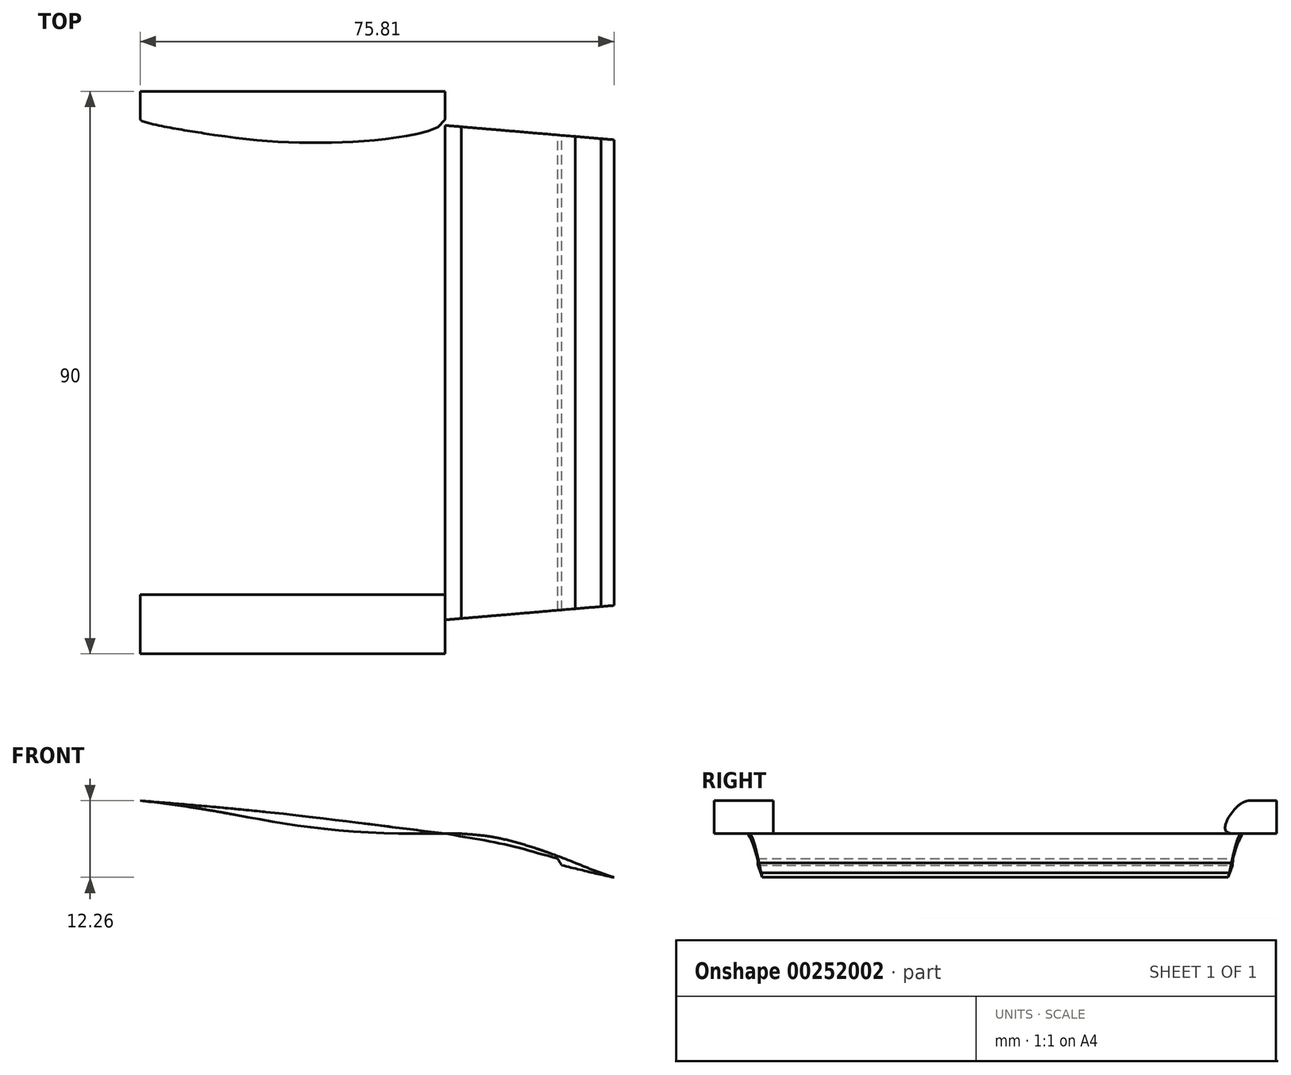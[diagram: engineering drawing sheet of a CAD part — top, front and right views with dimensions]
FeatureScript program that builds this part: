
annotation { "Feature Type Name" : "Feature", "Feature Type Description" : "" }
export const myFeature = defineFeature(function(context is Context, id is Id, definition is map)
    precondition{}
    {
        {
            var Q0;
            Q0=qCreatedBy(makeId("Top.planeOp"),FACE);
            var sketch = newSketch(context, id + "F0", { "sketchPlane" : qUnion([Q0])});
            skLineSegment(sketch, "E0.left", {"start": v(51.5, 37) * mm, "end": v(51.5, -37) * mm});
            skLineSegment(sketch, "E0.right", {"start": v(-51.5, 37) * mm, "end": v(-51.5, 35) * mm});
            skPoint(sketch, "E0.middle", {"position": v(0, 0) * mm});
            skLineSegment(sketch, "E1.bottom", {"start": v(-51.5, 35) * mm, "end": v(-24.5, 35) * mm});
            skLineSegment(sketch, "E1.top", {"start": v(-51.5, -35) * mm, "end": v(-24.5, -35) * mm});
            skLineSegment(sketch, "E1.right", {"start": v(-24.5, 35) * mm, "end": v(-24.5, -35) * mm});
            skPoint(sketch, "E1.middle", {"position": v(-38, 0) * mm});
            skLineSegment(sketch, "E2.trimOffspring", {"start": v(-51.5, -35) * mm, "end": v(-51.5, -37) * mm});
            skLineSegment(sketch, "E3", {"start": v(-36.5, 44.5) * mm, "end": v(51.5, 37) * mm});
            skLineSegment(sketch, "E4", {"start": v(-36.5, -44.5) * mm, "end": v(51.5, -37) * mm});
            skLineSegment(sketch, "E5", {"start": v(-36.5, 44.5) * mm, "end": v(-51.5, 44.5) * mm});
            skLineSegment(sketch, "E6", {"start": v(-51.5, 44.5) * mm, "end": v(-51.5, 37) * mm});
            skLineSegment(sketch, "E7", {"start": v(-51.5, -37) * mm, "end": v(-51.5, -44.5) * mm});
            skLineSegment(sketch, "E8", {"start": v(-51.5, -44.5) * mm, "end": v(-36.5, -44.5) * mm});
            skSolve(sketch);
        }
        {
            var Q0;
            Q0=makeQuery(id+"F0.imprint","IMPRINT",FACE,{"disambiguationData":[TD([[makeQuery(id+"F0.imprint","IMPRINT",EDGE,{"derivedFrom":sQuery(id+"F0.wireOp",EDGE,"E0.left")}),-1.0]])]});
            extrude(context, id + "F1", {"entities" : qUnion([Q0]), "endBound" : BoundingType.SYMMETRIC, "depth" : 40 * mm});
        }
        {
            var Q0;
            Q0=qCreatedBy(makeId("Front.planeOp"),FACE);
            var sketch = newSketch(context, id + "F2", { "sketchPlane" : qUnion([Q0])});
            skLineSegment(sketch, "E9", {"start": v(-51.5, -30.88) * mm, "end": v(-51.5, 38.27) * mm, "construction": true});
            skArc(sketch, "E10", {"start": v(-35.08, 14.93) * mm, "mid": v(-51.27, -2.64) * mm, "end": v(-30, -13.52) * mm});
            skLineSegment(sketch, "E11", {"start": v(21.5, 0) * mm, "end": v(66.36, 0) * mm, "construction": true});
            skLineSegment(sketch, "E12", {"start": v(21.5, 29.58) * mm, "end": v(21.5, -38.08) * mm, "construction": true});
            skLineSegment(sketch, "E13", {"start": v(13.3, 4) * mm, "end": v(21.47, 4) * mm, "construction": true});
            skLineSegment(sketch, "E14", {"start": v(39.5, 24.03) * mm, "end": v(39.5, -41.22) * mm, "construction": true});
            skPoint(sketch, "E15.orphan", {"position": v(0, 0) * mm});
            skFitSpline(sketch, "E16", {"points": [v(-31.64, -14.2) * mm, v(21.5, 4) * mm], "startDerivative": vector(84.94, 34.81) * mm, "endDerivative": vector(74.48, 19.76) * mm});
            skFitSpline(sketch, "E17", {"points": [v(21.5, 4) * mm, v(39.5, 0) * mm], "startDerivative": vector(28.2, -4.73) * mm, "endDerivative": vector(25.8, -7.27) * mm});
            skArc(sketch, "E18", {"start": v(50.52, -2.49) * mm, "mid": v(51.49, -0.27) * mm, "end": v(50.14, 1.73) * mm});
            skArc(sketch, "E19", {"start": v(39.5, 0) * mm, "mid": v(44.43, -3.82) * mm, "end": v(50.52, -2.49) * mm});
            skPoint(sketch, "E19.second.point", {"position": v(50.23, -2.7) * mm});
            skPoint(sketch, "E19.third.point", {"position": v(51.49, 8.31) * mm});
            skLineSegment(sketch, "E20", {"start": v(10.87, 9) * mm, "end": v(35.57, 9) * mm, "construction": true});
            skFitSpline(sketch, "E21.0", {"points": [v(21.5, 4) * mm, v(24.08, 4) * mm, v(28.98, 3.5) * mm, v(35.82, 1.7) * mm, v(42.27, -0.66) * mm, v(46.42, -2.27) * mm, v(48.5, -3) * mm]});
            skFitSpline(sketch, "E21.1", {"points": [v(-35.45, 9.95) * mm, v(-31.94, 9.69) * mm, v(-25.87, 9.12) * mm, v(-18.84, 8.18) * mm, v(-13.14, 7.2) * mm, v(-7.95, 6.24) * mm, v(-2.55, 5.34) * mm, v(3.68, 4.6) * mm, v(11.32, 4.12) * mm, v(17.8, 4) * mm, v(21.5, 4) * mm]});
            skFitSpline(sketch, "E22.trimOffspring", {"points": [v(21.5, 4) * mm, v(24.08, 4) * mm, v(28.98, 3.5) * mm, v(35.82, 1.7) * mm, v(42.27, -0.66) * mm, v(46.42, -2.27) * mm, v(48.5, -3) * mm, v(21.5, 4) * mm]});
            skLineSegment(sketch, "E23", {"start": v(-21.5, 30.5) * mm, "end": v(-21.5, -32.58) * mm, "construction": true});
            skLineSegment(sketch, "E24", {"start": v(-16.5, 19.65) * mm, "end": v(-16.5, 3.36) * mm, "construction": true});
            skLineSegment(sketch, "E25", {"start": v(-21.5, 13.8) * mm, "end": v(-17.04, 8.4) * mm});
            skFitSpline(sketch, "E26", {"points": [v(-35.08, 14.93) * mm, v(21.5, 9) * mm], "startDerivative": vector(86.4, -7.05) * mm, "endDerivative": vector(83.38, -10.43) * mm});
            skFitSpline(sketch, "E27", {"points": [v(21.5, 9) * mm, v(50.14, 1.73) * mm], "startDerivative": vector(37.32, -4.67) * mm, "endDerivative": vector(8.35, -5.74) * mm});
            skFitSpline(sketch, "E28.trimOffspring", {"points": [v(-34.87, 9.89) * mm, v(-27.67, 9.3) * mm, v(-19.58, 8.64) * mm, v(-11.59, 7.9) * mm, v(-6.32, 7.37) * mm, v(-1.09, 6.8) * mm, v(6.73, 5.85) * mm, v(14.55, 4.87) * mm, v(21.5, 4) * mm]});
            skLineSegment(sketch, "E29.trimOffspring", {"start": v(21.5, 4) * mm, "end": v(34.75, 4) * mm, "construction": true});
            skSolve(sketch);
        }
        {
            var Q0;
            {var subQ0=sQuery(id+"F2.wireOp",EDGE,"E28.trimOffspring");Q0=makeQuery(id+"F2.imprint","IMPRINT",FACE,{"disambiguationData":[TD([[makeQuery(id+"F2.imprint","IMPRINT",EDGE,{"derivedFrom":subQ0}),-1.0]])]});}
            var Q1;
            Q1=makeQuery(id+"F2.imprint","IMPRINT",FACE,{"disambiguationData":[TD([[makeQuery(id+"F2.imprint","IMPRINT",EDGE,{"derivedFrom":sQuery(id+"F2.wireOp",EDGE,"E17")}),1.0]])]});
            extrude(context, id + "F3", {"entities" : qUnion([Q0, Q1]), "endBound" : BoundingType.SYMMETRIC, "depth" : 90 * mm});
        }
        {
            var Q0;
            Q0=makeQuery(id+"F1.opExtrude","SWEPT_BODY",BODY,{"disambiguationData":[OSD([sQuery(id+"F0.wireOp",EDGE,"E0.left"),sQuery(id+"F0.wireOp",EDGE,"E0.right"),sQuery(id+"F0.wireOp",EDGE,"E1.bottom"),sQuery(id+"F0.wireOp",EDGE,"E1.top"),sQuery(id+"F0.wireOp",EDGE,"E1.right"),sQuery(id+"F0.wireOp",EDGE,"E2.trimOffspring"),sQuery(id+"F0.wireOp",EDGE,"E3"),sQuery(id+"F0.wireOp",EDGE,"E4"),sQuery(id+"F0.wireOp",EDGE,"E5"),sQuery(id+"F0.wireOp",EDGE,"E6"),sQuery(id+"F0.wireOp",EDGE,"E7"),sQuery(id+"F0.wireOp",EDGE,"E8")])]});
            var Q1;
            Q1=makeQuery(id+"F3.opExtrude","SWEPT_BODY",BODY,{"disambiguationData":[OSD([sQuery(id+"F2.wireOp",EDGE,"E10"),sQuery(id+"F2.wireOp",EDGE,"E16"),sQuery(id+"F2.wireOp",EDGE,"E17"),sQuery(id+"F2.wireOp",EDGE,"E18"),sQuery(id+"F2.wireOp",EDGE,"E19"),sQuery(id+"F2.wireOp",EDGE,"15d79667-4b94-408e-8f36-41715205f070"),sQuery(id+"F2.wireOp",EDGE,"74bc5fd0-7af1-4538-94f5-d98413db5bcc")])]});
            booleanBodies(context, id + "F4", {"operationType" : BooleanOperationType.INTERSECTION, "tools" : qUnion([Q0, Q1])});
        }
        {
            var Q0;
            {var subQ0=sQuery(id+"F2.wireOp",EDGE,"E28.trimOffspring");Q0=makeQuery(id+"F2.imprint","IMPRINT",FACE,{"disambiguationData":[TD([[makeQuery(id+"F2.imprint","IMPRINT",EDGE,{"derivedFrom":subQ0}),-1.0]])]});}
            extrude(context, id + "F5", {"entities" : qUnion([Q0]), "operationType" : NewBodyOperationType.REMOVE, "endBound" : BoundingType.SYMMETRIC, "oppositeDirection" : true, "depth" : 71 * mm});
        }
        {
            var Q0;
            Q0=qCreatedBy(makeId("Front.planeOp"),FACE);
            var sketch = newSketch(context, id + "F6", { "sketchPlane" : qUnion([Q0])});
            skArc(sketch, "E30.0", {"start": v(-35.08, 14.93) * mm, "mid": v(-51.27, -2.64) * mm, "end": v(-30, -13.52) * mm});
            skLineSegment(sketch, "E31", {"start": v(-36.5, 0) * mm, "end": v(-62.57, 0) * mm, "construction": true});
            skLineSegment(sketch, "E32", {"start": v(-36.5, 0) * mm, "end": v(-67.58, -11.93) * mm, "construction": true});
            skLineSegment(sketch, "E33", {"start": v(-51.5, 0) * mm, "end": v(-50.5, -5.38) * mm, "construction": true});
            skArc(sketch, "E34", {"start": v(-24.55, 1.05) * mm, "mid": v(-25.3, 4.3) * mm, "end": v(-26.91, 7.22) * mm});
            skLineSegment(sketch, "E35", {"start": v(-36.5, 0) * mm, "end": v(-28.49, -18.8) * mm, "construction": true});
            skLineSegment(sketch, "E36", {"start": v(-25.29, 7.84) * mm, "end": v(-29.43, 6.25) * mm, "construction": true});
            skLineSegment(sketch, "E37", {"start": v(-23.12, 1.6) * mm, "end": v(-28.08, -0.3) * mm, "construction": true});
            skLineSegment(sketch, "E38", {"start": v(-54.32, -2.77) * mm, "end": v(-47.19, -0.03) * mm, "construction": true});
            skLineSegment(sketch, "E39", {"start": v(-44.94, -7.31) * mm, "end": v(-52.1, -10.06) * mm, "construction": true});
            skLineSegment(sketch, "E40", {"start": v(-51.4, -1.65) * mm, "end": v(-26.91, 7.22) * mm});
            skLineSegment(sketch, "E41", {"start": v(-24.55, 1.05) * mm, "end": v(-48.69, -8.75) * mm});
            skSolve(sketch);
        }
        {
            var Q0;
            Q0=makeQuery(id+"F6.imprint","IMPRINT",FACE,{"disambiguationData":[TD([[makeQuery(id+"F6.imprint","IMPRINT",EDGE,{"derivedFrom":sQuery(id+"F6.wireOp",EDGE,"E34")}),1.0]])]});
            extrude(context, id + "F7", {"entities" : qUnion([Q0]), "operationType" : NewBodyOperationType.REMOVE, "endBound" : BoundingType.SYMMETRIC, "oppositeDirection" : true, "depth" : 83.5 * mm});
        }
        {
            var Q0;
            Q0=sQuery(id+"F6.wireOp",EDGE,"E32");
            cPlane(context, id + "F8", {"entities" : qUnion([Q0]), "cplaneType" : CPlaneType.LINE_ANGLE, "offset" : 25 * mm, "angle" : 90 * degree, "width" : 150 * mm, "height" : 150 * mm});
        }
        {
            var Q0;
            Q0=qCreatedBy(id+"F8.planeOp",FACE);
            var sketch = newSketch(context, id + "F9", { "sketchPlane" : qUnion([Q0])});
            skLineSegment(sketch, "E42", {"start": v(-33.58, 0) * mm, "end": v(-33.58, -28.28) * mm, "construction": true});
            skLineSegment(sketch, "E43", {"start": v(-33.58, -39) * mm, "end": v(-33.58, 39) * mm, "construction": true});
            skCircle(sketch, "E44", {"center": v(-33.58, 39) * mm, "radius": 1.25 * mm});
            skCircle(sketch, "E45", {"center": v(-33.58, -39) * mm, "radius": 1.25 * mm});
            skSolve(sketch);
        }
        {
            var Q0;
            Q0 = qSketchRegion(id + "F9", true);
            extrude(context, id + "F10", {"entities" : qUnion([Q0]), "operationType" : NewBodyOperationType.REMOVE, "oppositeDirection" : true, "depth" : 25 * mm});
        }
        {
            var Q0;
            Q0=sQuery(id+"F6.wireOp",EDGE,"E35");
            cPlane(context, id + "F11", {"entities" : qUnion([Q0]), "cplaneType" : CPlaneType.LINE_ANGLE, "offset" : 25 * mm, "angle" : 0 * degree, "width" : 150 * mm, "height" : 150 * mm});
        }
        {
            var Q0;
            Q0=qCreatedBy(id+"F11.planeOp",FACE);
            var sketch = newSketch(context, id + "F12", { "sketchPlane" : qUnion([Q0])});
            skLineSegment(sketch, "E46", {"start": v(0, 14.3) * mm, "end": v(31.59, 14.3) * mm, "construction": true});
            skLineSegment(sketch, "E47", {"start": v(39, 14.3) * mm, "end": v(-39, 14.3) * mm, "construction": true});
            skLineSegment(sketch, "E48", {"start": v(39, 14.3) * mm, "end": v(39, -0.7) * mm, "construction": true});
            skLineSegment(sketch, "E49", {"start": v(-39, 14.3) * mm, "end": v(-39, -0.7) * mm, "construction": true});
            skLineSegment(sketch, "E50", {"start": v(39, 1.3) * mm, "end": v(36.5, 1.3) * mm});
            skLineSegment(sketch, "E51", {"start": v(36.5, 1.3) * mm, "end": v(36.5, -1.2) * mm});
            skLineSegment(sketch, "E52", {"start": v(39, 1.3) * mm, "end": v(39, -1.2) * mm});
            skLineSegment(sketch, "E53", {"start": v(39, -1.2) * mm, "end": v(36.5, -1.2) * mm});
            skLineSegment(sketch, "E54", {"start": v(-39, 1.3) * mm, "end": v(-36.5, 1.3) * mm});
            skLineSegment(sketch, "E55", {"start": v(-36.5, 1.3) * mm, "end": v(-36.5, -1.2) * mm});
            skLineSegment(sketch, "E56", {"start": v(-39, 1.3) * mm, "end": v(-39, -1.2) * mm});
            skLineSegment(sketch, "E57", {"start": v(-39, -1.2) * mm, "end": v(-36.5, -1.2) * mm});
            skSolve(sketch);
        }
        {
            var Q0;
            Q0=makeQuery(id+"F12.imprint","IMPRINT",FACE,{"disambiguationData":[TD([[makeQuery(id+"F12.imprint","IMPRINT",EDGE,{"derivedFrom":sQuery(id+"F12.wireOp",EDGE,"E50")}),1.0]])]});
            var Q1;
            Q1=sQuery(id+"F12.wireOp",EDGE,"E48");
            revolve(context, id + "F13", {"operationType" : NewBodyOperationType.REMOVE, "entities" : qUnion([Q0]), "axis" : qUnion([Q1]), "revolveType" : RevolveType.FULL, "oppositeDirection" : true});
        }
        {
            var Q0;
            Q0=makeQuery(id+"F12.imprint","IMPRINT",FACE,{"disambiguationData":[TD([[makeQuery(id+"F12.imprint","IMPRINT",EDGE,{"derivedFrom":sQuery(id+"F12.wireOp",EDGE,"E54")}),-1.0]])]});
            var Q1;
            Q1=sQuery(id+"F12.wireOp",EDGE,"E49");
            revolve(context, id + "F14", {"operationType" : NewBodyOperationType.REMOVE, "entities" : qUnion([Q0]), "axis" : qUnion([Q1]), "revolveType" : RevolveType.FULL, "oppositeDirection" : true});
        }
        {
            var Q0;
            Q0=makeQuery(id+"F5.boolean.opBoolean","COPY",EDGE,{"derivedFrom":makeQuery(id+"F5.opExtrude","CAP_EDGE",EDGE,{"disambiguationData":[OSD([sQuery(id+"F2.wireOp",EDGE,"E28.trimOffspring")])],"isStart":false})});
            var Q1;
            Q1=makeQuery(id+"F5.boolean.opBoolean","COPY",EDGE,{"derivedFrom":makeQuery(id+"F5.opExtrude","CAP_EDGE",EDGE,{"disambiguationData":[OSD([sQuery(id+"F2.wireOp",EDGE,"E25")])],"isStart":false})});
            var Q2;
            Q2=makeQuery(id+"F5.boolean.opBoolean","COPY",EDGE,{"derivedFrom":makeQuery(id+"F5.opExtrude","CAP_EDGE",EDGE,{"disambiguationData":[OSD([sQuery(id+"F2.wireOp",EDGE,"E28.trimOffspring")])],"isStart":true})});
            var Q3;
            Q3=makeQuery(id+"F5.boolean.opBoolean","COPY",EDGE,{"derivedFrom":makeQuery(id+"F5.opExtrude","CAP_EDGE",EDGE,{"disambiguationData":[OSD([sQuery(id+"F2.wireOp",EDGE,"E25")])],"isStart":true})});
            fillet(context, id + "F15", {"entities" : qUnion([Q0, Q1, Q2, Q3]), "radius" : 5 * mm, "tangentPropagation" : true, "allowEdgeOverflow" : false});
        }
    });
